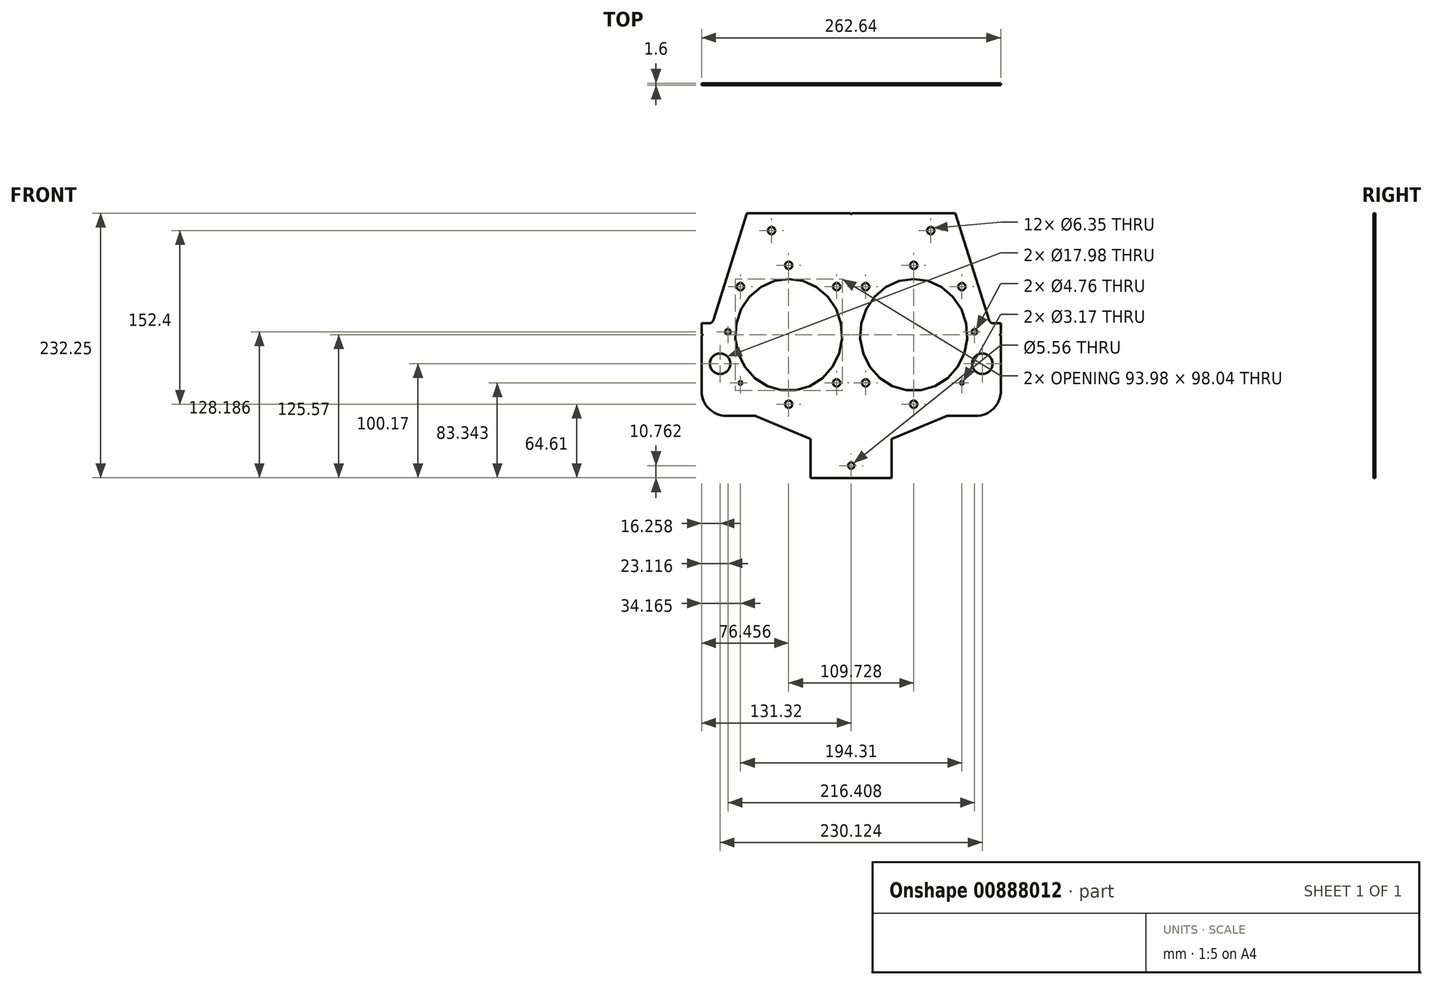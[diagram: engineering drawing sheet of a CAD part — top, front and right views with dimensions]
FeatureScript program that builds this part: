
annotation { "Feature Type Name" : "Feature", "Feature Type Description" : "" }
export const myFeature = defineFeature(function(context is Context, id is Id, definition is map)
    precondition{}
    {
        {
            var Q0;
            Q0=qCreatedBy(makeId("Front.planeOp"),FACE);
            var sketch = newSketch(context, id + "F0", { "sketchPlane" : qUnion([Q0])});
            skLineSegment(sketch, "E0", {"start": v(0, 106.68) * mm, "end": v(-91.44, 106.68) * mm});
            skLineSegment(sketch, "E1", {"start": v(-91.44, 106.68) * mm, "end": v(-121.22, 12.38) * mm});
            skLineSegment(sketch, "E2", {"start": v(-124.25, 10.16) * mm, "end": v(-131.32, 10.16) * mm});
            skLineSegment(sketch, "E3", {"start": v(-131.32, 10.16) * mm, "end": v(-131.32, -49.28) * mm});
            skLineSegment(sketch, "E4", {"start": v(-109.47, -71.12) * mm, "end": v(-84.71, -71.12) * mm});
            skLineSegment(sketch, "E5", {"start": v(-83.49, -71.37) * mm, "end": v(-35.56, -91.44) * mm});
            skLineSegment(sketch, "E6", {"start": v(-35.56, -91.44) * mm, "end": v(-35.56, -125.57) * mm});
            skLineSegment(sketch, "E7", {"start": v(-35.56, -125.57) * mm, "end": v(0, -125.57) * mm});
            skPoint(sketch, "E8.visualSharp", {"position": v(-131.32, -71.12) * mm});
            skArc(sketch, "E8.filletArc", {"start": v(-131.32, -49.28) * mm, "mid": v(-124.92, -64.72) * mm, "end": v(-109.47, -71.12) * mm});
            skLineSegment(sketch, "E9.MirrorCS", {"start": v(124.25, 10.16) * mm, "end": v(131.32, 10.16) * mm});
            skLineSegment(sketch, "E10.MirrorCS", {"start": v(35.56, -91.44) * mm, "end": v(35.56, -125.57) * mm});
            skLineSegment(sketch, "E11.MirrorCS", {"start": v(0, 106.68) * mm, "end": v(91.44, 106.68) * mm});
            skLineSegment(sketch, "E12.MirrorCS", {"start": v(35.56, -125.57) * mm, "end": v(0, -125.57) * mm});
            skPoint(sketch, "E13.MirrorP", {"position": v(131.32, -71.12) * mm});
            skLineSegment(sketch, "E14.MirrorCS", {"start": v(131.32, 10.16) * mm, "end": v(131.32, -49.28) * mm});
            skLineSegment(sketch, "E15.MirrorCS", {"start": v(83.49, -71.37) * mm, "end": v(35.56, -91.44) * mm});
            skLineSegment(sketch, "E16.MirrorCS", {"start": v(109.47, -71.12) * mm, "end": v(84.71, -71.12) * mm});
            skLineSegment(sketch, "E17.MirrorCS", {"start": v(91.44, 106.68) * mm, "end": v(121.22, 12.38) * mm});
            skArc(sketch, "E18.MirrorCS", {"start": v(131.32, -49.28) * mm, "mid": v(124.92, -64.72) * mm, "end": v(109.47, -71.12) * mm});
            skPoint(sketch, "E19.visualSharp", {"position": v(-121.92, 10.16) * mm});
            skArc(sketch, "E19.filletArc", {"start": v(-124.25, 10.16) * mm, "mid": v(-122.37, 10.77) * mm, "end": v(-121.22, 12.38) * mm});
            skPoint(sketch, "E20.visualSharp", {"position": v(121.92, 10.16) * mm});
            skArc(sketch, "E20.filletArc", {"start": v(121.22, 12.38) * mm, "mid": v(122.37, 10.77) * mm, "end": v(124.25, 10.16) * mm});
            skPoint(sketch, "E21.visualSharp", {"position": v(84.07, -71.12) * mm});
            skArc(sketch, "E21.filletArc", {"start": v(84.71, -71.12) * mm, "mid": v(84.09, -71.18) * mm, "end": v(83.49, -71.37) * mm});
            skPoint(sketch, "E22.visualSharp", {"position": v(-84.07, -71.12) * mm});
            skArc(sketch, "E22.filletArc", {"start": v(-83.49, -71.37) * mm, "mid": v(-84.09, -71.18) * mm, "end": v(-84.71, -71.12) * mm});
            skSolve(sketch);
        }
        {
            var Q0;
            Q0=qCreatedBy(makeId("Front.planeOp"),FACE);
            var sketch = newSketch(context, id + "F1", { "sketchPlane" : qUnion([Q0])});
            skCircle(sketch, "E23", {"center": v(-115.06, -25.4) * mm, "radius": 9 * mm});
            skCircle(sketch, "E24", {"center": v(-69.85, 91.44) * mm, "radius": 3.18 * mm});
            skCircle(sketch, "E25", {"center": v(-97.16, 42.23) * mm, "radius": 3.18 * mm});
            skCircle(sketch, "E26", {"center": v(-97.16, -42.23) * mm, "radius": 1.59 * mm});
            skCircle(sketch, "E27", {"center": v(-12.7, 42.23) * mm, "radius": 3.18 * mm});
            skCircle(sketch, "E28", {"center": v(-12.7, -42.23) * mm, "radius": 3.18 * mm});
            skCircle(sketch, "E29", {"center": v(0, -114.8) * mm, "radius": 2.78 * mm});
            skCircle(sketch, "E30", {"center": v(-108.2, 2.62) * mm, "radius": 2.38 * mm});
            skCircle(sketch, "E31.MirrorC", {"center": v(97.16, -42.23) * mm, "radius": 1.59 * mm});
            skCircle(sketch, "E32.MirrorC", {"center": v(108.2, 2.62) * mm, "radius": 2.38 * mm});
            skCircle(sketch, "E33.MirrorC", {"center": v(69.85, 91.44) * mm, "radius": 3.18 * mm});
            skCircle(sketch, "E34.MirrorC", {"center": v(12.7, -42.23) * mm, "radius": 3.18 * mm});
            skCircle(sketch, "E35.MirrorC", {"center": v(97.16, 42.23) * mm, "radius": 3.18 * mm});
            skCircle(sketch, "E36.MirrorC", {"center": v(12.7, 42.23) * mm, "radius": 3.18 * mm});
            skCircle(sketch, "E37.MirrorC", {"center": v(115.06, -25.4) * mm, "radius": 9 * mm});
            skCircle(sketch, "E38", {"center": v(0, 106.84) * mm, "radius": 0.8 * mm});
            skCircle(sketch, "E39", {"center": v(-131.24, 0) * mm, "radius": 0.8 * mm});
            skCircle(sketch, "E40", {"center": v(131.35, 0) * mm, "radius": 0.8 * mm});
            skEllipse(sketch, "E41", {"center": v(54.86, 0) * mm, "majorRadius": 49.02 * mm, "minorRadius": 47 * mm, "majorAxis": v(0, 1)});
            skEllipse(sketch, "E42", {"center": v(-54.86, 0) * mm, "majorRadius": 49.02 * mm, "minorRadius": 47 * mm, "majorAxis": v(0, 1)});
            skSolve(sketch);
        }
        {
            var Q0;
            Q0 = qSketchRegion(id + "F0", true);
            extrude(context, id + "F2", {"entities" : qUnion([Q0]), "depth" : 1.6 * mm, "offsetDistance" : 25.4 * mm});
        }
        {
            var Q0;
            Q0 = qSketchRegion(id + "F1", true);
            extrude(context, id + "F3", {"entities" : qUnion([Q0]), "operationType" : NewBodyOperationType.REMOVE, "oppositeDirection" : true, "depth" : -1.6 * mm, "offsetDistance" : 25.4 * mm});
        }
        {
            var Q0;
            Q0=makeQuery(id+"F1.imprint","IMPRINT",FACE,{"disambiguationData":[TD([[makeQuery(id+"F1.imprint","IMPRINT",EDGE,{"derivedFrom":sQuery(id+"F1.wireOp",EDGE,"E42")}),1.0]])]});
            var sketch = newSketch(context, id + "F4", { "sketchPlane" : qUnion([Q0])});
            skCircle(sketch, "E43", {"center": v(-54.86, 60.96) * mm, "radius": 3.18 * mm});
            skCircle(sketch, "E44.MirrorC", {"center": v(-54.86, -60.96) * mm, "radius": 3.18 * mm});
            skCircle(sketch, "E45.MirrorC", {"center": v(54.86, -60.96) * mm, "radius": 3.18 * mm});
            skCircle(sketch, "E46.MirrorC", {"center": v(54.86, 60.96) * mm, "radius": 3.18 * mm});
            skSolve(sketch);
        }
        {
            var Q0;
            Q0 = qSketchRegion(id + "F4", true);
            extrude(context, id + "F5", {"entities" : qUnion([Q0]), "operationType" : NewBodyOperationType.REMOVE, "depth" : 4.14 * mm, "offsetDistance" : 25.4 * mm});
        }
    });
